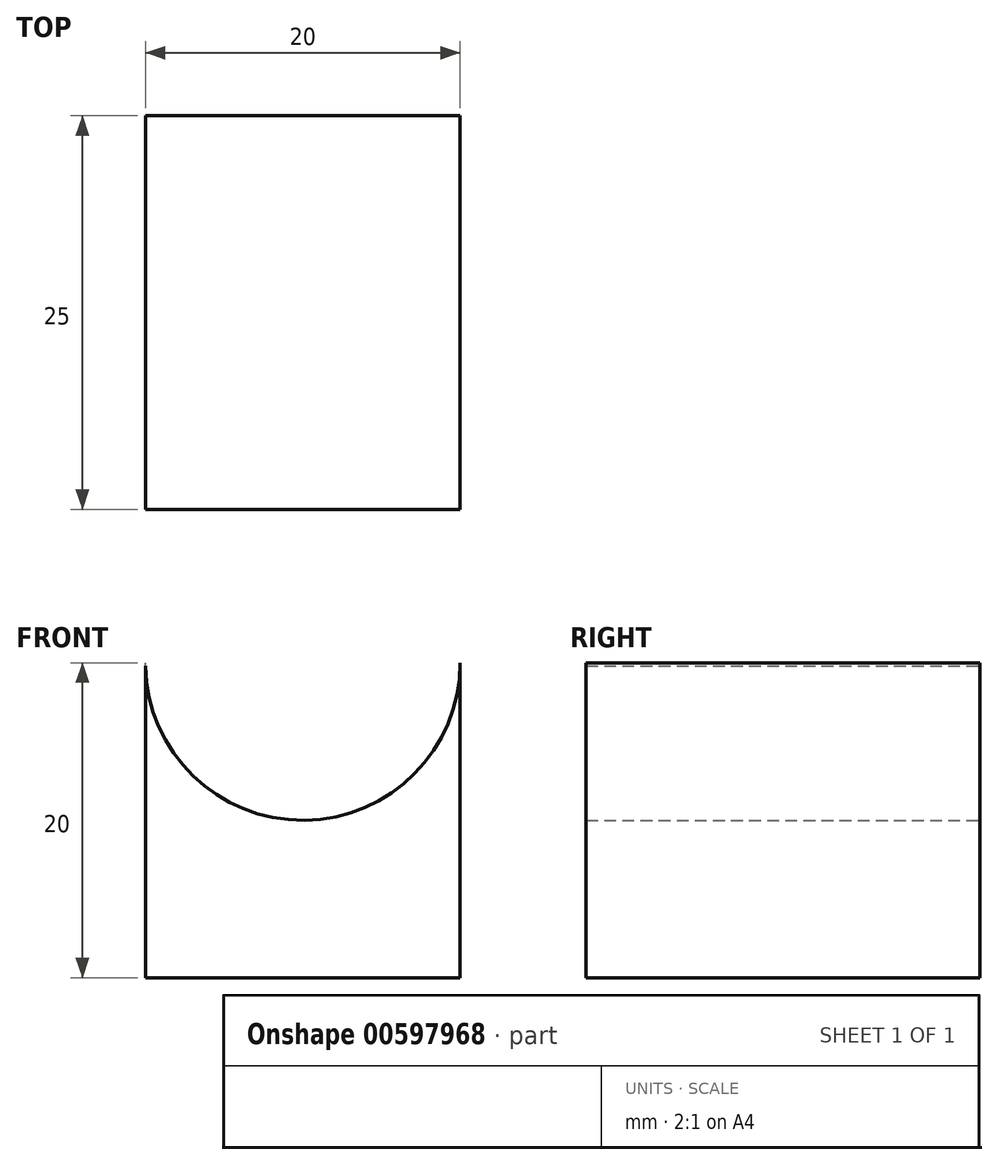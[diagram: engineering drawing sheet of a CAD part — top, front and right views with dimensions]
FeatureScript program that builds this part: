
annotation { "Feature Type Name" : "Feature", "Feature Type Description" : "" }
export const myFeature = defineFeature(function(context is Context, id is Id, definition is map)
    precondition{}
    {
        {
            var Q0;
            Q0=qCreatedBy(makeId("Front.planeOp"),FACE);
            var sketch = newSketch(context, id + "F0", { "sketchPlane" : qUnion([Q0])});
            skArc(sketch, "E0", {"start": v(-10, 0) * mm, "mid": v(0, -10) * mm, "end": v(10, 0) * mm});
            skLineSegment(sketch, "E1", {"start": v(0, -10) * mm, "end": v(0, -20) * mm});
            skPoint(sketch, "E2.start.orphan", {"position": v(-10, 0) * mm});
            skLineSegment(sketch, "E3", {"start": v(-10, 0) * mm, "end": v(-10, -0.2) * mm});
            skLineSegment(sketch, "E4", {"start": v(0, -20) * mm, "end": v(-10, -20) * mm});
            skLineSegment(sketch, "E5", {"start": v(-10, -0.2) * mm, "end": v(-10, -20) * mm});
            skLineSegment(sketch, "E6", {"start": v(0, -20) * mm, "end": v(10, -20) * mm});
            skLineSegment(sketch, "E7", {"start": v(10, 0) * mm, "end": v(10, -20) * mm});
            skSolve(sketch);
        }
        {
            var Q0;
            Q0 = qSketchRegion(id + "F0", true);
            extrude(context, id + "F1", {"entities" : qUnion([Q0]), "depth" : 25 * mm, "offsetDistance" : 25 * mm});
        }
    });
